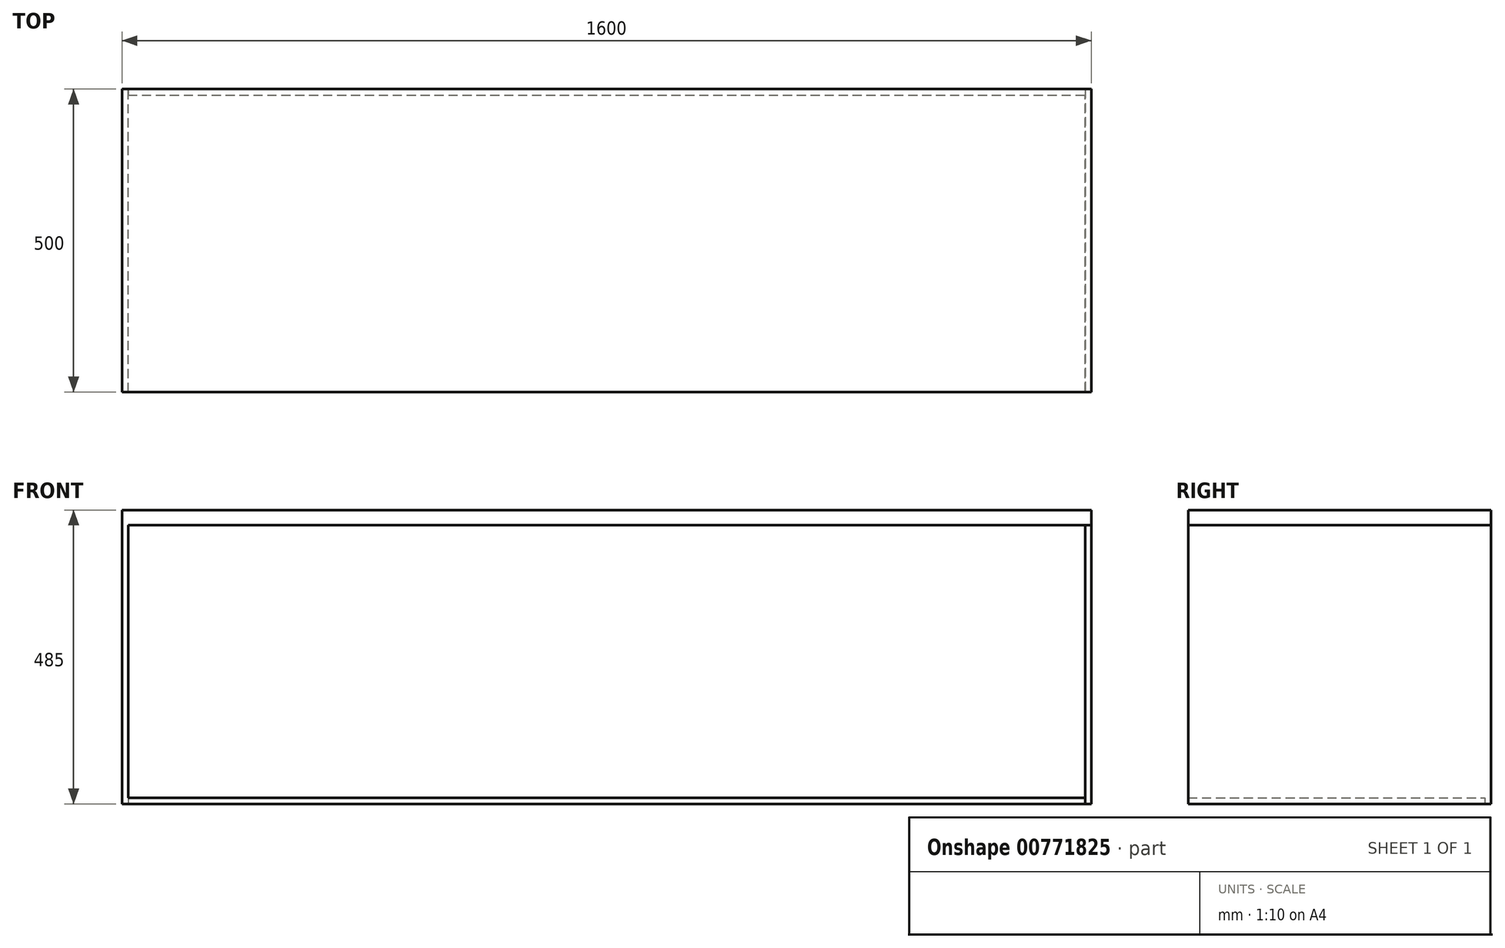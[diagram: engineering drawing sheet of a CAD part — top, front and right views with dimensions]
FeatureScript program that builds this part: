
annotation { "Feature Type Name" : "Feature", "Feature Type Description" : "" }
export const myFeature = defineFeature(function(context is Context, id is Id, definition is map)
    precondition{}
    {
        {
            var Q0;
            Q0=qCreatedBy(makeId("Top.planeOp"),FACE);
            var sketch = newSketch(context, id + "F0", { "sketchPlane" : qUnion([Q0])});
            skLineSegment(sketch, "E0.bottom", {"start": v(0, 0) * mm, "end": v(1600, 0) * mm});
            skLineSegment(sketch, "E0.top", {"start": v(0, 500) * mm, "end": v(1600, 500) * mm});
            skLineSegment(sketch, "E0.left", {"start": v(0, 0) * mm, "end": v(0, 500) * mm});
            skLineSegment(sketch, "E0.right", {"start": v(1600, 0) * mm, "end": v(1600, 500) * mm});
            skSolve(sketch);
        }
        {
            var Q0;
            Q0=makeQuery(id+"F0.imprint","IMPRINT",FACE,{"disambiguationData":[TD([[makeQuery(id+"F0.imprint","IMPRINT",EDGE,{"derivedFrom":sQuery(id+"F0.wireOp",EDGE,"E0.bottom")}),1.0]])]});
            extrude(context, id + "F1", {"entities" : qUnion([Q0]), "depth" : 25 * mm, "offsetDistance" : 25 * mm});
        }
        {
            var Q0;
            Q0=makeQuery(id+"F0.imprint","IMPRINT",FACE,{"disambiguationData":[TD([[makeQuery(id+"F0.imprint","IMPRINT",EDGE,{"derivedFrom":sQuery(id+"F0.wireOp",EDGE,"E0.bottom")}),1.0]])]});
            cPlane(context, id + "F2", {"entities" : qUnion([Q0]), "cplaneType" : CPlaneType.OFFSET, "offset" : 460 * mm, "oppositeDirection" : true, "width" : 150 * mm, "height" : 150 * mm});
        }
        {
            var Q0;
            Q0=qCreatedBy(id+"F2.planeOp",FACE);
            var sketch = newSketch(context, id + "F3", { "sketchPlane" : qUnion([Q0])});
            skLineSegment(sketch, "E1.bottom", {"start": v(10, 0) * mm, "end": v(1590, 0) * mm});
            skLineSegment(sketch, "E1.top", {"start": v(10, 490) * mm, "end": v(1590, 490) * mm});
            skLineSegment(sketch, "E1.left", {"start": v(10, 0) * mm, "end": v(10, 490) * mm});
            skLineSegment(sketch, "E1.right", {"start": v(1590, 0) * mm, "end": v(1590, 490) * mm});
            skSolve(sketch);
        }
        {
            var Q0;
            Q0=makeQuery(id+"F3.imprint","IMPRINT",FACE,{"disambiguationData":[TD([[makeQuery(id+"F3.imprint","IMPRINT",EDGE,{"derivedFrom":sQuery(id+"F3.wireOp",EDGE,"E1.bottom")}),1.0]])]});
            extrude(context, id + "F4", {"entities" : qUnion([Q0]), "depth" : 10 * mm, "offsetDistance" : 25 * mm});
        }
        {
            var Q0;
            Q0=makeQuery(id+"F0.imprint","IMPRINT",FACE,{"disambiguationData":[TD([[makeQuery(id+"F0.imprint","IMPRINT",EDGE,{"derivedFrom":sQuery(id+"F0.wireOp",EDGE,"E0.bottom")}),1.0]])]});
            var sketch = newSketch(context, id + "F5", { "sketchPlane" : qUnion([Q0])});
            skLineSegment(sketch, "E2.bottom", {"start": v(0, 0) * mm, "end": v(10, 0) * mm});
            skLineSegment(sketch, "E2.top", {"start": v(0, 500) * mm, "end": v(10, 500) * mm});
            skLineSegment(sketch, "E2.left", {"start": v(0, 0) * mm, "end": v(0, 500) * mm});
            skLineSegment(sketch, "E2.right", {"start": v(10, 0) * mm, "end": v(10, 500) * mm});
            skSolve(sketch);
        }
        {
            var Q0;
            Q0=qSketchRegion(id+"F5",true);
            var Q1;
            Q1=makeQuery(id+"F4.opExtrude","CAP_FACE",FACE,{"disambiguationData":[OSD([sQuery(id+"F3.wireOp",EDGE,"E1.bottom"),sQuery(id+"F3.wireOp",EDGE,"E1.top"),sQuery(id+"F3.wireOp",EDGE,"E1.left"),sQuery(id+"F3.wireOp",EDGE,"E1.right")])],"isStart":true});
            extrude(context, id + "F6", {"entities" : qUnion([Q0]), "operationType" : NewBodyOperationType.ADD, "endBound" : BoundingType.UP_TO_SURFACE, "oppositeDirection" : true, "depth" : 25 * mm, "endBoundEntityFace" : qUnion([Q1]), "offsetDistance" : 25 * mm});
        }
        {
            var Q0;
            Q0=makeQuery(id+"F0.imprint","IMPRINT",FACE,{"disambiguationData":[TD([[makeQuery(id+"F0.imprint","IMPRINT",EDGE,{"derivedFrom":sQuery(id+"F0.wireOp",EDGE,"E0.bottom")}),1.0]])]});
            var sketch = newSketch(context, id + "F7", { "sketchPlane" : qUnion([Q0])});
            skLineSegment(sketch, "E3.bottom", {"start": v(1600, 0) * mm, "end": v(1590, 0) * mm});
            skLineSegment(sketch, "E3.top", {"start": v(1600, 500) * mm, "end": v(1590, 500) * mm});
            skLineSegment(sketch, "E3.left", {"start": v(1600, 0) * mm, "end": v(1600, 500) * mm});
            skLineSegment(sketch, "E3.right", {"start": v(1590, 0) * mm, "end": v(1590, 500) * mm});
            skSolve(sketch);
        }
        {
            var Q0;
            Q0=makeQuery(id+"F7.imprint","IMPRINT",FACE,{"disambiguationData":[TD([[makeQuery(id+"F7.imprint","IMPRINT",EDGE,{"derivedFrom":sQuery(id+"F7.wireOp",EDGE,"E3.bottom")}),1.0]])]});
            var Q1;
            Q1=makeQuery(id+"F4.opExtrude","CAP_FACE",FACE,{"disambiguationData":[OSD([sQuery(id+"F3.wireOp",EDGE,"E1.bottom"),sQuery(id+"F3.wireOp",EDGE,"E1.top"),sQuery(id+"F3.wireOp",EDGE,"E1.left"),sQuery(id+"F3.wireOp",EDGE,"E1.right")])],"isStart":true});
            extrude(context, id + "F8", {"entities" : qUnion([Q0]), "endBound" : BoundingType.UP_TO_SURFACE, "oppositeDirection" : true, "depth" : 25 * mm, "endBoundEntityFace" : qUnion([Q1]), "offsetDistance" : 25 * mm});
        }
    });
